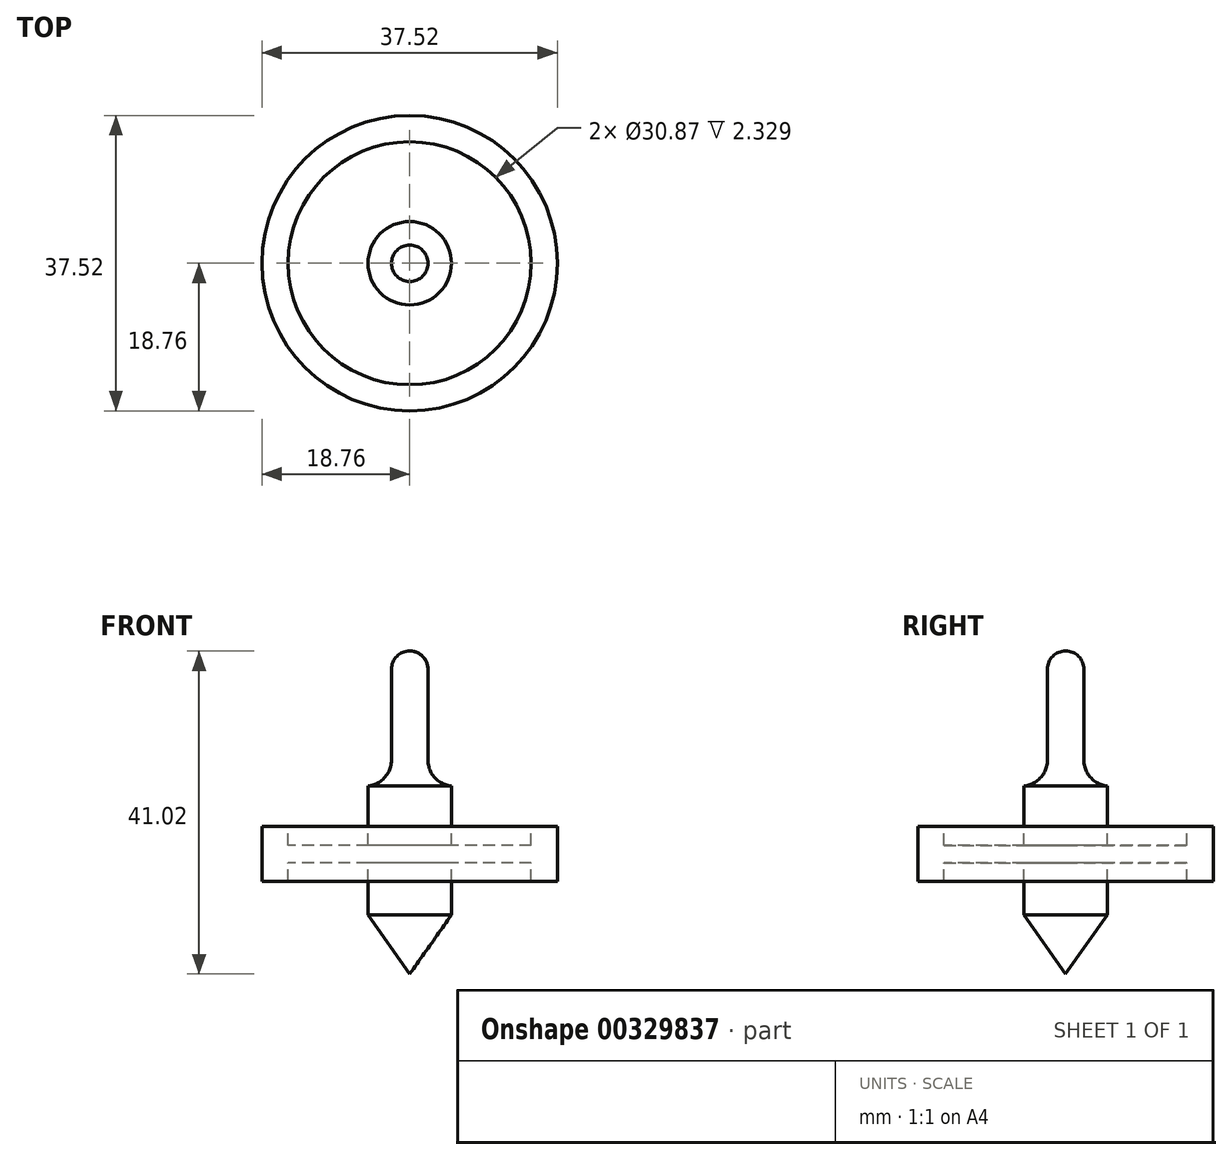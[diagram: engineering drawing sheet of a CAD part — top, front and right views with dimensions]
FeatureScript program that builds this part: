
annotation { "Feature Type Name" : "Feature", "Feature Type Description" : "" }
export const myFeature = defineFeature(function(context is Context, id is Id, definition is map)
    precondition{}
    {
        {
            var Q0;
            Q0=qCreatedBy(makeId("Front.planeOp"),FACE);
            var sketch = newSketch(context, id + "F0", { "sketchPlane" : qUnion([Q0])});
            skLineSegment(sketch, "E0", {"start": v(0, 0) * mm, "end": v(5.3, 7.48) * mm});
            skLineSegment(sketch, "E1", {"start": v(5.3, 7.48) * mm, "end": v(5.3, 14.1) * mm});
            skArc(sketch, "E2", {"start": v(2.32, 27.16) * mm, "mid": v(3.17, 24.95) * mm, "end": v(5.3, 23.89) * mm});
            skLineSegment(sketch, "E3", {"start": v(2.32, 27.16) * mm, "end": v(2.32, 38.7) * mm});
            skArc(sketch, "E4", {"start": v(2.32, 38.7) * mm, "mid": v(1.64, 40.34) * mm, "end": v(0, 41.02) * mm});
            skLineSegment(sketch, "E5", {"start": v(0, 41.02) * mm, "end": v(0, 0) * mm});
            skLineSegment(sketch, "E6", {"start": v(5.3, 14.1) * mm, "end": v(15.44, 14.1) * mm});
            skLineSegment(sketch, "E7", {"start": v(15.44, 14.1) * mm, "end": v(15.44, 11.77) * mm});
            skLineSegment(sketch, "E8", {"start": v(15.44, 11.77) * mm, "end": v(18.76, 11.77) * mm});
            skLineSegment(sketch, "E9", {"start": v(18.76, 11.77) * mm, "end": v(18.76, 18.74) * mm});
            skLineSegment(sketch, "E10", {"start": v(18.76, 18.74) * mm, "end": v(15.44, 18.67) * mm});
            skLineSegment(sketch, "E11", {"start": v(15.44, 18.67) * mm, "end": v(15.44, 16.34) * mm});
            skLineSegment(sketch, "E12", {"start": v(15.44, 16.34) * mm, "end": v(5.3, 16.34) * mm});
            skLineSegment(sketch, "E13.trimOffspring", {"start": v(5.3, 16.34) * mm, "end": v(5.3, 23.89) * mm});
            skSolve(sketch);
        }
        {
            var Q0;
            {var subQ4=sQuery(id+"F0.wireOp",EDGE,"E0");Q0=makeQuery(id+"F0.imprint","IMPRINT",FACE,{"disambiguationData":[TD([[makeQuery(id+"F0.imprint","IMPRINT",EDGE,{"derivedFrom":subQ4}),1.0]])]});}
            var Q1;
            Q1=sQuery(id+"F0.wireOp",EDGE,"E5");
            revolve(context, id + "F1", {"entities" : qUnion([Q0]), "axis" : qUnion([Q1]), "revolveType" : RevolveType.FULL});
        }
    });
